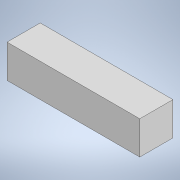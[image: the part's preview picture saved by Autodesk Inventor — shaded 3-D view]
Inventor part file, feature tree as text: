
AUTODESK INVENTOR PART (.ipt)
format: ipt  version: 2022 (Build 260153000, 153)  size: 90,112 bytes
history: native  units: in
note: dims shown in document units (in); Inventor stores cm internally (conversion verified against a paired STEP export)
features: extrude x1, sketch x1
ambient origin geometry x8: Origin, YZ Plane, XZ Plane, XY Plane, X Axis, Y Axis, Z Axis, Center Point
bodies: Body1 (feature_tree)
feature tree (2):
  extrude  "Extrusion2"  Depth=0.4in
  sketch  "Sketch1"  dims[d6=0.05in d7=0.05in d8=0.05in d9=0.05in d10=0.4in d11=0.0in]
